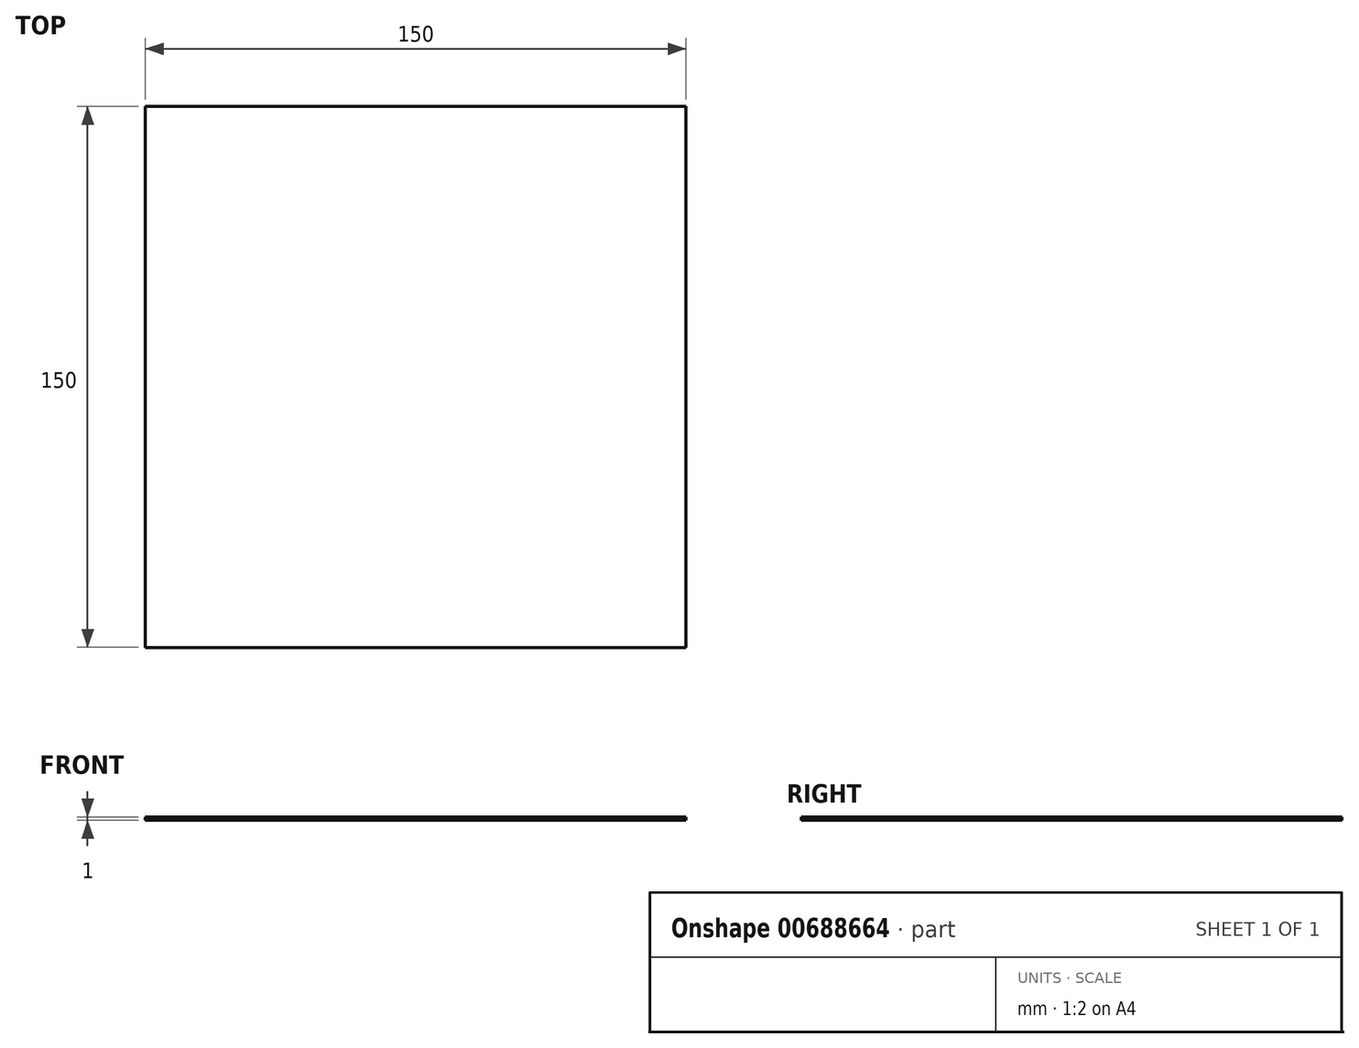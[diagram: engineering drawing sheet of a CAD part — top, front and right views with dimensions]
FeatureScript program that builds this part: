
annotation { "Feature Type Name" : "Feature", "Feature Type Description" : "" }
export const myFeature = defineFeature(function(context is Context, id is Id, definition is map)
    precondition{}
    {
        {
            var Q0;
            Q0=qCreatedBy(makeId("Top.planeOp"),FACE);
            var sketch = newSketch(context, id + "F0", { "sketchPlane" : qUnion([Q0])});
            skLineSegment(sketch, "E0.bottom", {"start": v(-102.5, 51.57) * mm, "end": v(47.5, 51.57) * mm});
            skLineSegment(sketch, "E0.top", {"start": v(-102.5, -98.43) * mm, "end": v(47.5, -98.43) * mm});
            skLineSegment(sketch, "E0.left", {"start": v(-102.5, 51.57) * mm, "end": v(-102.5, -98.43) * mm});
            skLineSegment(sketch, "E0.right", {"start": v(47.5, 51.57) * mm, "end": v(47.5, -98.43) * mm});
            skSolve(sketch);
        }
        {
            var Q0;
            Q0=makeQuery(id+"F0.imprint","IMPRINT",FACE,{"disambiguationData":[TD([[makeQuery(id+"F0.imprint","IMPRINT",EDGE,{"derivedFrom":sQuery(id+"F0.wireOp",EDGE,"E0.bottom")}),-1.0]])]});
            var Q1;
            Q1=sQuery(id+"F0.wireOp",EDGE,"E0.right");
            var Q2;
            Q2=sQuery(id+"F0.wireOp",EDGE,"E0.top");
            var Q3;
            Q3=sQuery(id+"F0.wireOp",EDGE,"E0.left");
            var Q4;
            Q4=sQuery(id+"F0.wireOp",EDGE,"E0.bottom");
            extrude(context, id + "F1", {"entities" : qUnion([Q0]), "surfaceEntities" : qUnion([Q1, Q2, Q3, Q4]), "depth" : 1 * mm, "offsetDistance" : 25 * mm});
        }
    });
